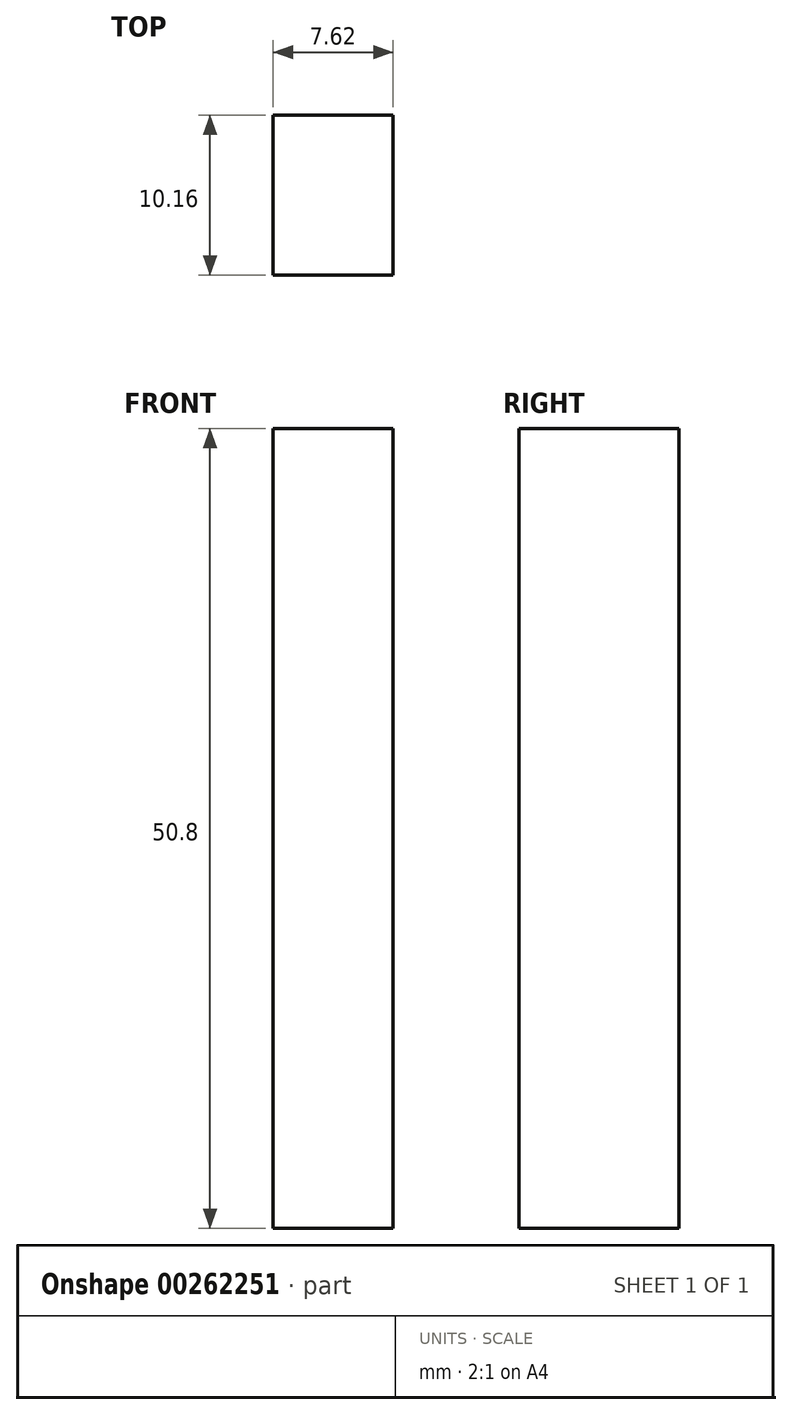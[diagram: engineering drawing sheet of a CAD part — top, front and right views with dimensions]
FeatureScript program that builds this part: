
annotation { "Feature Type Name" : "Feature", "Feature Type Description" : "" }
export const myFeature = defineFeature(function(context is Context, id is Id, definition is map)
    precondition{}
    {
        {
            var Q0;
            Q0=qCreatedBy(makeId("Front.planeOp"),FACE);
            var sketch = newSketch(context, id + "F0", { "sketchPlane" : qUnion([Q0])});
            skLineSegment(sketch, "E0.bottom", {"start": v(-51.13, 46.78) * mm, "end": v(-43.5, 46.78) * mm});
            skLineSegment(sketch, "E0.top", {"start": v(-51.13, -4.02) * mm, "end": v(-43.5, -4.02) * mm});
            skLineSegment(sketch, "E0.left", {"start": v(-51.13, 46.78) * mm, "end": v(-51.13, -4.02) * mm});
            skLineSegment(sketch, "E0.right", {"start": v(-43.5, 46.78) * mm, "end": v(-43.5, -4.02) * mm});
            skSolve(sketch);
        }
        {
            var Q0;
            Q0=makeQuery(id+"F0.imprint","IMPRINT",FACE,{"disambiguationData":[TD([[makeQuery(id+"F0.imprint","IMPRINT",EDGE,{"derivedFrom":sQuery(id+"F0.wireOp",EDGE,"E0.bottom")}),-1.0]])]});
            extrude(context, id + "F1", {"entities" : qUnion([Q0]), "depth" : 10.16 * mm});
        }
    });
